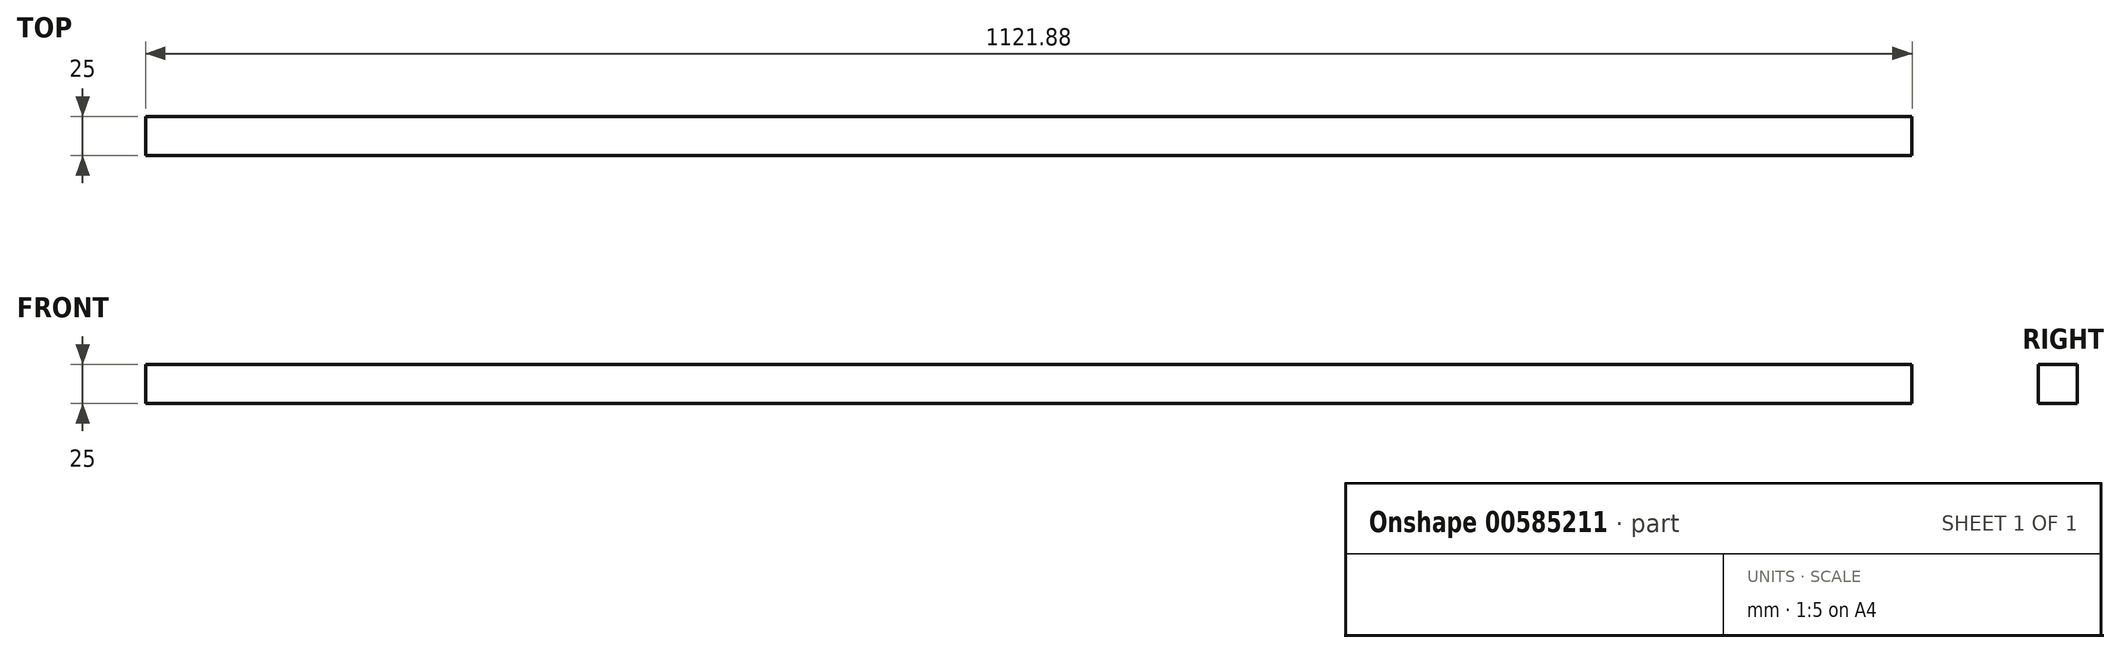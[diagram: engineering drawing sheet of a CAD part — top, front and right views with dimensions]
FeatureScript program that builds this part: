
annotation { "Feature Type Name" : "Feature", "Feature Type Description" : "" }
export const myFeature = defineFeature(function(context is Context, id is Id, definition is map)
    precondition{}
    {
        {
            var Q0;
            Q0=qCreatedBy(makeId("Front.planeOp"),FACE);
            var sketch = newSketch(context, id + "F0", { "sketchPlane" : qUnion([Q0])});
            skLineSegment(sketch, "E0.bottom", {"start": v(0, 0) * mm, "end": v(1121.88, 0) * mm});
            skLineSegment(sketch, "E0.top", {"start": v(0, 25) * mm, "end": v(1121.88, 25) * mm});
            skLineSegment(sketch, "E0.left", {"start": v(0, 0) * mm, "end": v(0, 25) * mm});
            skLineSegment(sketch, "E0.right", {"start": v(1121.88, 0) * mm, "end": v(1121.88, 25) * mm});
            skSolve(sketch);
        }
        {
            var Q0;
            Q0=makeQuery(id+"F0.imprint","IMPRINT",FACE,{"disambiguationData":[TD([[makeQuery(id+"F0.imprint","IMPRINT",EDGE,{"derivedFrom":sQuery(id+"F0.wireOp",EDGE,"E0.bottom")}),1.0]])]});
            extrude(context, id + "F1", {"entities" : qUnion([Q0]), "endBound" : BoundingType.SYMMETRIC, "depth" : 25 * mm, "offsetDistance" : 25 * mm});
        }
    });
